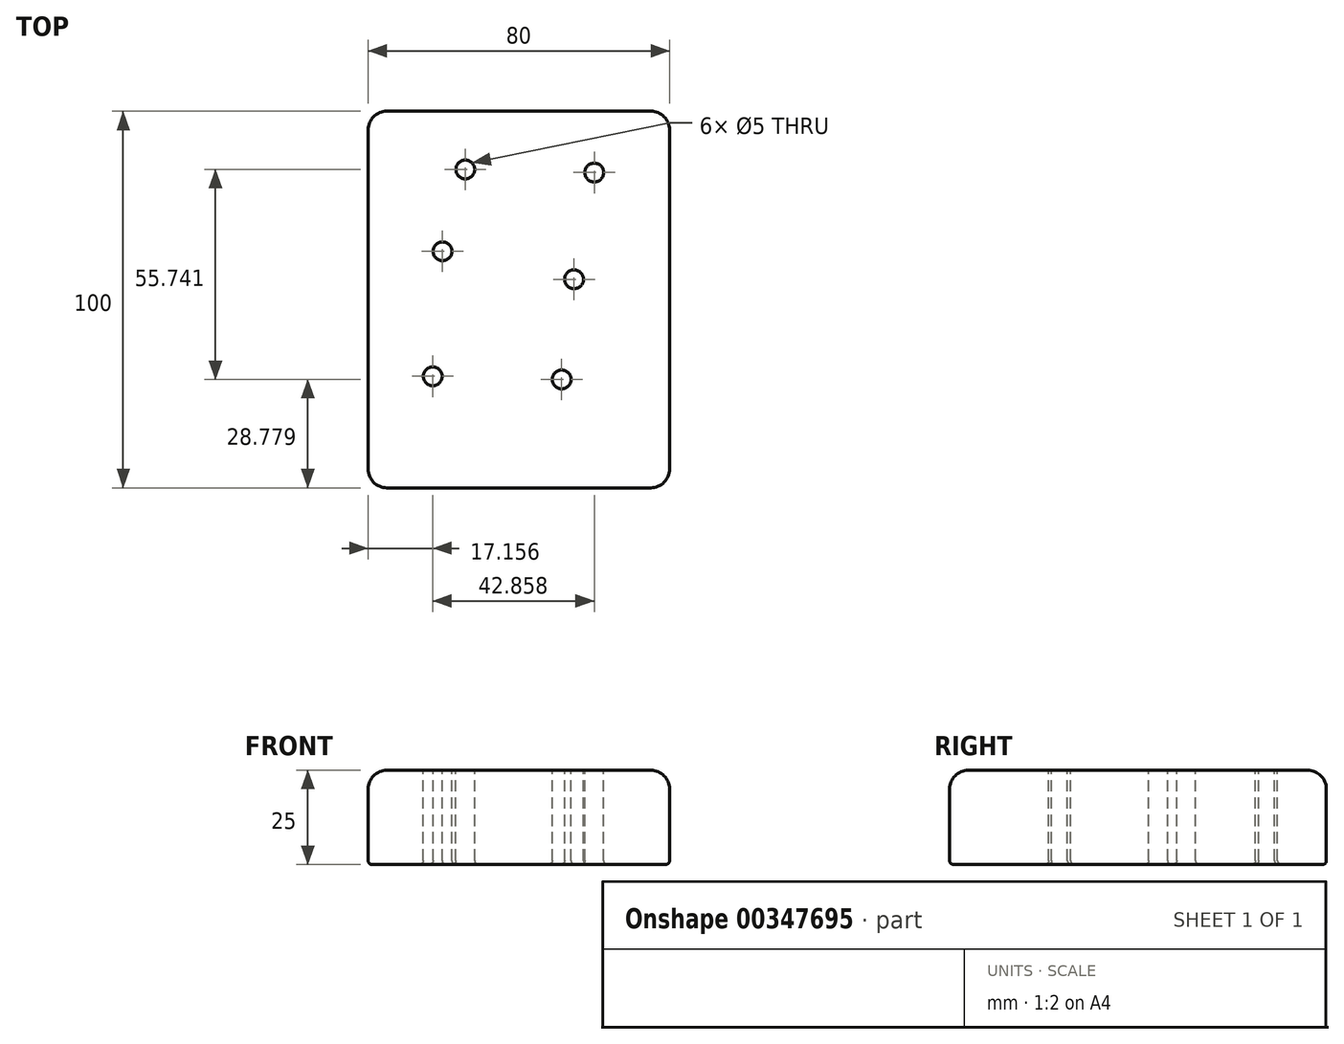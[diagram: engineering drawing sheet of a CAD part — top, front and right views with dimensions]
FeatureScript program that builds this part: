
annotation { "Feature Type Name" : "Feature", "Feature Type Description" : "" }
export const myFeature = defineFeature(function(context is Context, id is Id, definition is map)
    precondition{}
    {
        {
            var Q0;
            Q0=qCreatedBy(makeId("Top.planeOp"),FACE);
            var sketch = newSketch(context, id + "F0", { "sketchPlane" : qUnion([Q0])});
            skLineSegment(sketch, "E0.bottom", {"start": v(-40, -50) * mm, "end": v(40, -50) * mm});
            skLineSegment(sketch, "E0.top", {"start": v(-40, 50) * mm, "end": v(40, 50) * mm});
            skLineSegment(sketch, "E0.left", {"start": v(-40, -50) * mm, "end": v(-40, 50) * mm});
            skLineSegment(sketch, "E0.right", {"start": v(40, -50) * mm, "end": v(40, 50) * mm});
            skPoint(sketch, "E0.middle", {"position": v(0, 0) * mm});
            skSolve(sketch);
        }
        {
            var Q0;
            Q0=makeQuery(id+"F0.imprint","IMPRINT",FACE,{"disambiguationData":[TD([[makeQuery(id+"F0.imprint","IMPRINT",EDGE,{"derivedFrom":sQuery(id+"F0.wireOp",EDGE,"E0.bottom")}),1.0]])]});
            extrude(context, id + "F1", {"entities" : qUnion([Q0]), "depth" : 25 * mm});
        }
        {
            var Q0;
            Q0=makeQuery(id+"F1.opExtrude","CAP_FACE",FACE,{"disambiguationData":[OSD([sQuery(id+"F0.wireOp",EDGE,"E0.bottom"),sQuery(id+"F0.wireOp",EDGE,"E0.top"),sQuery(id+"F0.wireOp",EDGE,"E0.left"),sQuery(id+"F0.wireOp",EDGE,"E0.right")])],"isStart":false});
            var sketch = newSketch(context, id + "F2", { "sketchPlane" : qUnion([Q0])});
            skPoint(sketch, "E1", {"position": v(20.01, 33.7) * mm});
            skPoint(sketch, "E2", {"position": v(-14.2, 34.52) * mm});
            skPoint(sketch, "E3", {"position": v(14.65, 5.35) * mm});
            skPoint(sketch, "E4", {"position": v(-20.25, 12.78) * mm});
            skPoint(sketch, "E5", {"position": v(-22.84, -20.4) * mm});
            skPoint(sketch, "E6", {"position": v(11.37, -21.22) * mm});
            skSolve(sketch);
        }
        {
            var Q0;
            Q0=sQuery(id+"F2.wireOp",VERTEX,"E1");
            var Q1;
            Q1=sQuery(id+"F2.wireOp",VERTEX,"E2");
            var Q2;
            Q2=sQuery(id+"F2.wireOp",VERTEX,"E4");
            var Q3;
            Q3=sQuery(id+"F2.wireOp",VERTEX,"E3");
            var Q4;
            Q4=sQuery(id+"F2.wireOp",VERTEX,"E6");
            var Q5;
            Q5=sQuery(id+"F2.wireOp",VERTEX,"E5");
            var Q6;
            Q6=makeQuery(id+"F1.opExtrude","SWEPT_BODY",BODY,{"disambiguationData":[OSD([sQuery(id+"F0.wireOp",EDGE,"E0.bottom"),sQuery(id+"F0.wireOp",EDGE,"E0.top"),sQuery(id+"F0.wireOp",EDGE,"E0.left"),sQuery(id+"F0.wireOp",EDGE,"E0.right")])]});
            hole(context, id + "F3", {"style" : HoleStyle.SIMPLE, "endStyle" : HoleEndStyle.THROUGH, "holeDiameter" : 5 * mm, "isTappedThrough" : true, "tappedDepth" : 12 * mm, "tapClearance" : 3, "locations" : qUnion([Q0, Q1, Q2, Q3, Q4, Q5]), "scope" : qUnion([Q6])});
        }
        {
            var Q0;
            Q0=makeQuery(id+"F1.opExtrude","CAP_EDGE",EDGE,{"disambiguationData":[OSD([sQuery(id+"F0.wireOp",EDGE,"E0.left")])],"isStart":false});
            var Q1;
            Q1=makeQuery(id+"F1.opExtrude","CAP_EDGE",EDGE,{"disambiguationData":[OSD([sQuery(id+"F0.wireOp",EDGE,"E0.top")])],"isStart":false});
            var Q2;
            Q2=makeQuery(id+"F1.opExtrude","CAP_EDGE",EDGE,{"disambiguationData":[OSD([sQuery(id+"F0.wireOp",EDGE,"E0.right")])],"isStart":false});
            var Q3;
            Q3=makeQuery(id+"F1.opExtrude","CAP_EDGE",EDGE,{"disambiguationData":[OSD([sQuery(id+"F0.wireOp",EDGE,"E0.bottom")])],"isStart":false});
            var Q4;
            Q4=makeQuery(id+"F1.opExtrude","SWEPT_EDGE",EDGE,{"disambiguationData":[OSD([sQuery(id+"F0.wireOp",EDGE,"E0.top"),sQuery(id+"F0.wireOp",EDGE,"E0.left")])]});
            var Q5;
            Q5=makeQuery(id+"F1.opExtrude","SWEPT_EDGE",EDGE,{"disambiguationData":[OSD([sQuery(id+"F0.wireOp",EDGE,"E0.bottom"),sQuery(id+"F0.wireOp",EDGE,"E0.left")])]});
            var Q6;
            Q6=makeQuery(id+"F1.opExtrude","SWEPT_EDGE",EDGE,{"disambiguationData":[OSD([sQuery(id+"F0.wireOp",EDGE,"E0.bottom"),sQuery(id+"F0.wireOp",EDGE,"E0.right")])]});
            var Q7;
            Q7=makeQuery(id+"F1.opExtrude","SWEPT_EDGE",EDGE,{"disambiguationData":[OSD([sQuery(id+"F0.wireOp",EDGE,"E0.top"),sQuery(id+"F0.wireOp",EDGE,"E0.right")])]});
            fillet(context, id + "F4", {"entities" : qUnion([Q0, Q1, Q2, Q3, Q4, Q5, Q6, Q7]), "radius" : 5 * mm, "tangentPropagation" : true, "allowEdgeOverflow" : false});
        }
        {
            var Q0;
            Q0=makeQuery(id+"F1.opExtrude","CAP_FACE",FACE,{"disambiguationData":[OSD([sQuery(id+"F0.wireOp",EDGE,"E0.bottom"),sQuery(id+"F0.wireOp",EDGE,"E0.top"),sQuery(id+"F0.wireOp",EDGE,"E0.left"),sQuery(id+"F0.wireOp",EDGE,"E0.right")])],"isStart":true});
            fillet(context, id + "F5", {"entities" : qUnion([Q0]), "radius" : 1 * mm, "tangentPropagation" : true, "allowEdgeOverflow" : false});
        }
    });
